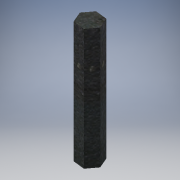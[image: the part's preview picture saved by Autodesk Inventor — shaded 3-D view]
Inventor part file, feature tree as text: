
AUTODESK INVENTOR PART (.ipt)
format: ipt  version: 2016 (Build 200138000, 138)  size: 100,864 bytes
history: native  units: in
note: dims shown in document units (in); Inventor stores cm internally (conversion verified against a paired STEP export)
features: extrude x1, sketch x1
ambient origin geometry x8: Origin, YZ Plane, XZ Plane, XY Plane, X Axis, Y Axis, Z Axis, Center Point
bodies: Solid1 (feature_tree)
feature tree (2):
  extrude  "Extrusion1"  Depth=3.0in TaperAngle=0.0deg
  sketch  "Sketch1"  dims[d0=0.5in d1=3.0in d2=0.0in]
